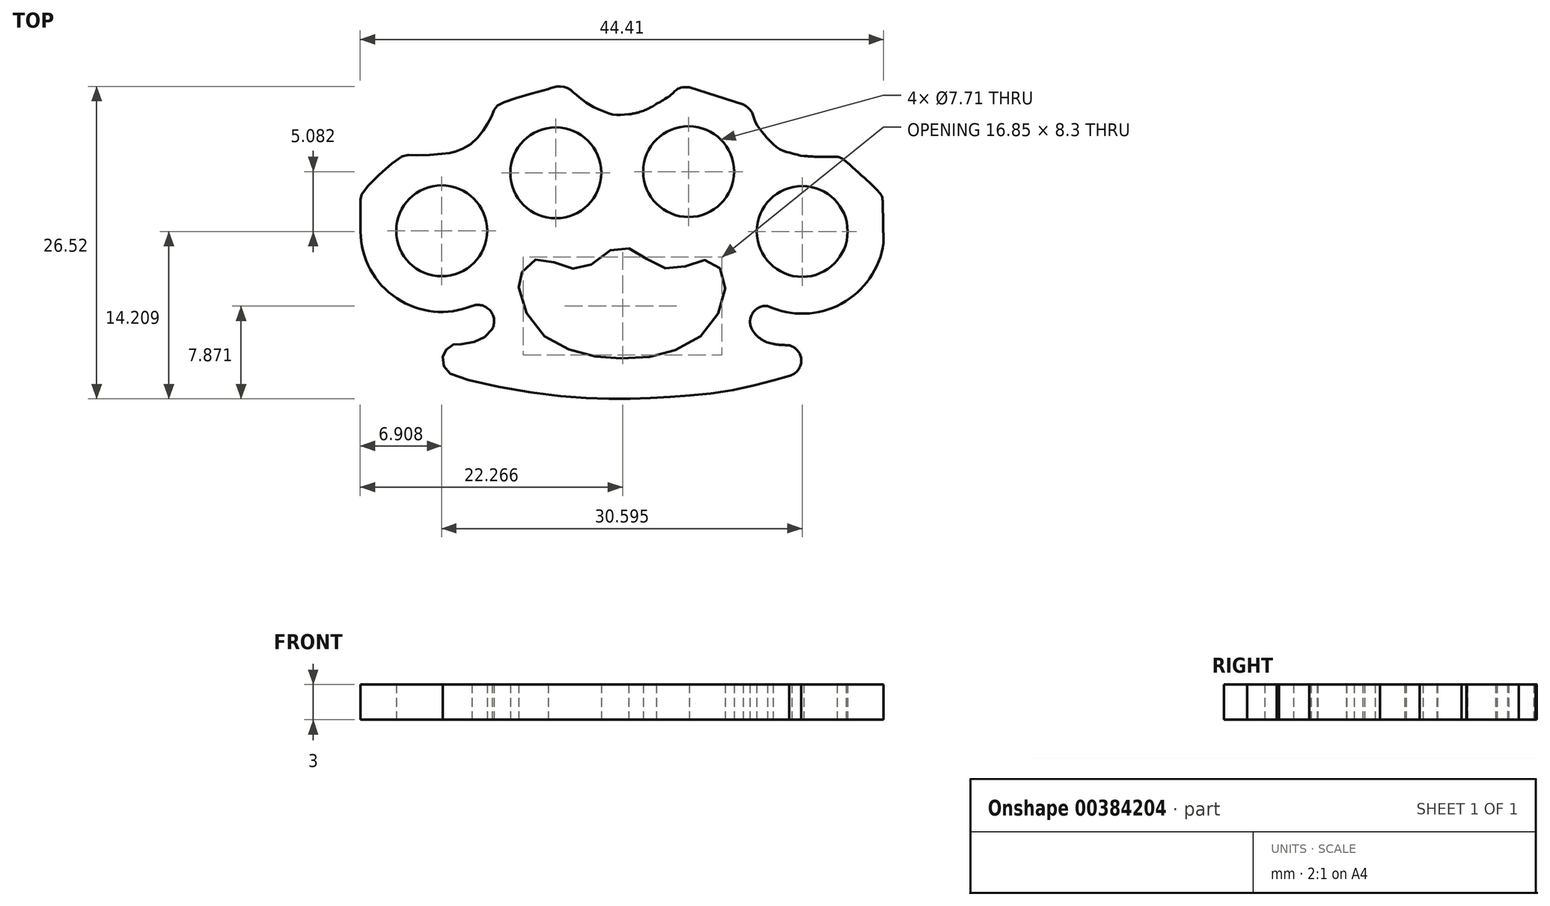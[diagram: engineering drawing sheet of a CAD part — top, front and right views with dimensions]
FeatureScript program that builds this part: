
annotation { "Feature Type Name" : "Feature", "Feature Type Description" : "" }
export const myFeature = defineFeature(function(context is Context, id is Id, definition is map)
    precondition{}
    {
        {
            var Q0;
            Q0=qCreatedBy(makeId("Top.planeOp"),FACE);
            var sketch = newSketch(context, id + "F0", { "sketchPlane" : qUnion([Q0])});
            skCircle(sketch, "E0", {"center": v(-53.62, 27.4) * mm, "radius": 3.86 * mm});
            skCircle(sketch, "E1", {"center": v(-43.94, 32.31) * mm, "radius": 3.86 * mm});
            skCircle(sketch, "E2", {"center": v(-32.66, 32.42) * mm, "radius": 3.86 * mm});
            skCircle(sketch, "E3", {"center": v(-23.03, 27.34) * mm, "radius": 3.86 * mm});
            skArc(sketch, "E4", {"start": v(-16.12, 26.36) * mm, "mid": v(-19.7, 21.2) * mm, "end": v(-25.98, 21.01) * mm});
            skArc(sketch, "E5", {"start": v(-60.5, 27.34) * mm, "mid": v(-57.45, 21.67) * mm, "end": v(-51.04, 21.01) * mm});
            skLineSegment(sketch, "E6", {"start": v(-60.5, 27.34) * mm, "end": v(-60.53, 30) * mm});
            skFitSpline(sketch, "E7", {"points": [v(-60.53, 30) * mm, v(-60.23, 30.76) * mm, v(-57.06, 33.67) * mm, v(-56.16, 33.8) * mm, v(-53.46, 33.94) * mm, v(-52.59, 34.1) * mm, v(-51.42, 34.57) * mm, v(-50.23, 35.74) * mm, v(-49.52, 36.85) * mm, v(-49.12, 37.75) * mm, v(-48.59, 38.2) * mm, v(-44.57, 39.41) * mm], "startDerivative": vector(0.99, 9.25) * mm, "endDerivative": vector(33.85, 9.01) * mm});
            skFitSpline(sketch, "E8", {"points": [v(-44.57, 39.41) * mm, v(-43.98, 39.61) * mm, v(-43.06, 39.56) * mm, v(-42.25, 38.98) * mm, v(-41.25, 38.21) * mm, v(-40.04, 37.6) * mm, v(-38.94, 37.25) * mm, v(-37.74, 37.28) * mm], "startDerivative": vector(4.96, 2.1) * mm, "endDerivative": vector(8.03, 0.8) * mm});
            skFitSpline(sketch, "E9", {"points": [v(-37.74, 37.28) * mm, v(-37.05, 37.4) * mm, v(-36.14, 37.74) * mm, v(-35.38, 38.18) * mm], "startDerivative": vector(2.19, 0.31) * mm, "endDerivative": vector(2.12, 1.36) * mm});
            skFitSpline(sketch, "E10", {"points": [v(-35.38, 38.18) * mm, v(-35, 38.4) * mm, v(-34.4, 38.76) * mm, v(-33.96, 39.12) * mm, v(-33.68, 39.38) * mm, v(-33.2, 39.57) * mm, v(-32.6, 39.57) * mm], "startDerivative": vector(2.41, 1.25) * mm, "endDerivative": vector(3.42, -0.26) * mm});
            skLineSegment(sketch, "E11", {"start": v(-32.6, 39.57) * mm, "end": v(-28.03, 38.13) * mm});
            skFitSpline(sketch, "E12", {"points": [v(-28.03, 38.13) * mm, v(-27.6, 37.83) * mm, v(-27.23, 37.3) * mm, v(-27, 36.63) * mm, v(-26.55, 35.96) * mm, v(-26, 35.26) * mm, v(-25.11, 34.44) * mm, v(-24.4, 34.1) * mm, v(-23.64, 33.9) * mm, v(-22.88, 33.73) * mm], "startDerivative": vector(4.82, -2.87) * mm, "endDerivative": vector(6.35, -0.82) * mm});
            skFitSpline(sketch, "E13", {"points": [v(-22.88, 33.73) * mm, v(-22.66, 33.73) * mm, v(-20.05, 33.69) * mm], "startDerivative": vector(0.66, 0) * mm, "endDerivative": vector(9.86, 0.1) * mm});
            skFitSpline(sketch, "E14", {"points": [v(-20.05, 33.69) * mm, v(-19.66, 33.54) * mm, v(-19.3, 33.27) * mm], "startDerivative": vector(0.82, -0.25) * mm, "endDerivative": vector(0.68, -0.58) * mm});
            skFitSpline(sketch, "E15", {"points": [v(-19.3, 33.27) * mm, v(-16.44, 30.6) * mm, v(-16.23, 30.2) * mm, v(-16.18, 29.73) * mm], "startDerivative": vector(6.22, -5.51) * mm, "endDerivative": vector(0.15, -2.45) * mm});
            skFitSpline(sketch, "E16", {"points": [v(-16.12, 26.36) * mm, v(-16.18, 29.73) * mm], "startDerivative": vector(-0.07, 3.37) * mm, "endDerivative": vector(-0.07, 3.37) * mm});
            skArc(sketch, "E17", {"start": v(-51.04, 21.01) * mm, "mid": v(-49.5, 20.61) * mm, "end": v(-49.35, 19.04) * mm});
            skArc(sketch, "E18", {"start": v(-25.98, 21.01) * mm, "mid": v(-27.25, 20.38) * mm, "end": v(-27.25, 18.95) * mm});
            skArc(sketch, "E19", {"start": v(-27.25, 18.95) * mm, "mid": v(-26.5, 18.18) * mm, "end": v(-25.5, 17.8) * mm});
            skLineSegment(sketch, "E20", {"start": v(42.52, 62.88) * mm, "end": v(42.52, 42.22) * mm});
            skArc(sketch, "E21", {"start": v(-23.92, 17.6) * mm, "mid": v(-23.11, 16.26) * mm, "end": v(-24.12, 15.08) * mm});
            skFitSpline(sketch, "E22", {"points": [v(-25.5, 17.8) * mm, v(-25.46, 17.78) * mm, v(-25.34, 17.76) * mm, v(-25.04, 17.72) * mm, v(-24.77, 17.7) * mm, v(-24.53, 17.7) * mm, v(-24.32, 17.68) * mm, v(-24.1, 17.66) * mm, v(-23.92, 17.6) * mm], "startDerivative": vector(0.65, -0.3) * mm, "endDerivative": vector(1.36, -0.67) * mm});
            skFitSpline(sketch, "E23", {"points": [v(-49.35, 19.04) * mm, v(-50, 18.35) * mm, v(-51, 17.94) * mm, v(-52.17, 17.77) * mm, v(-52.6, 17.75) * mm, v(-53.12, 17.43) * mm, v(-53.42, 16.98) * mm, v(-53.54, 16.44) * mm, v(-53.33, 15.69) * mm, v(-52.6, 15.13) * mm, v(-46.09, 13.69) * mm, v(-40.36, 13.16) * mm, v(-36.8, 13.15) * mm, v(-33.61, 13.33) * mm, v(-30.25, 13.65) * mm, v(-26.47, 14.42) * mm, v(-24.12, 15.08) * mm], "startDerivative": vector(-13.44, -16.95) * mm, "endDerivative": vector(30.51, 9.2) * mm});
            skFitSpline(sketch, "E24", {"points": [v(-40.92, 24.54) * mm, v(-39.62, 25.57) * mm, v(-38.59, 25.94) * mm, v(-37.58, 25.86) * mm, v(-36.55, 25.28) * mm, v(-35.52, 24.46) * mm, v(-34.33, 24.2) * mm, v(-33.24, 24.27) * mm, v(-32.08, 24.8) * mm, v(-31.02, 24.86) * mm, v(-30.3, 24.48) * mm, v(-29.7, 23.77) * mm, v(-29.6, 22.24) * mm, v(-30.15, 20.4) * mm, v(-31.52, 18.53) * mm, v(-33.64, 17.34) * mm, v(-35.44, 16.78) * mm, v(-37.72, 16.57) * mm, v(-39.75, 16.65) * mm, v(-41.53, 16.89) * mm, v(-43.78, 17.74) * mm, v(-45.42, 18.93) * mm, v(-46.74, 21.12) * mm, v(-47.09, 22.82) * mm, v(-47, 23.4) * mm, v(-46.66, 24.11) * mm, v(-46.03, 24.78) * mm, v(-44.94, 25.04) * mm, v(-44.02, 24.67) * mm, v(-42.96, 24.22) * mm, v(-41.8, 24.22) * mm, v(-40.92, 24.54) * mm]});
            skSolve(sketch);
        }
        {
            var Q0;
            Q0 = qSketchRegion(id + "F0", true);
            extrude(context, id + "F1", {"entities" : qUnion([Q0]), "depth" : 3 * mm, "offsetDistance" : 25 * mm});
        }
    });
